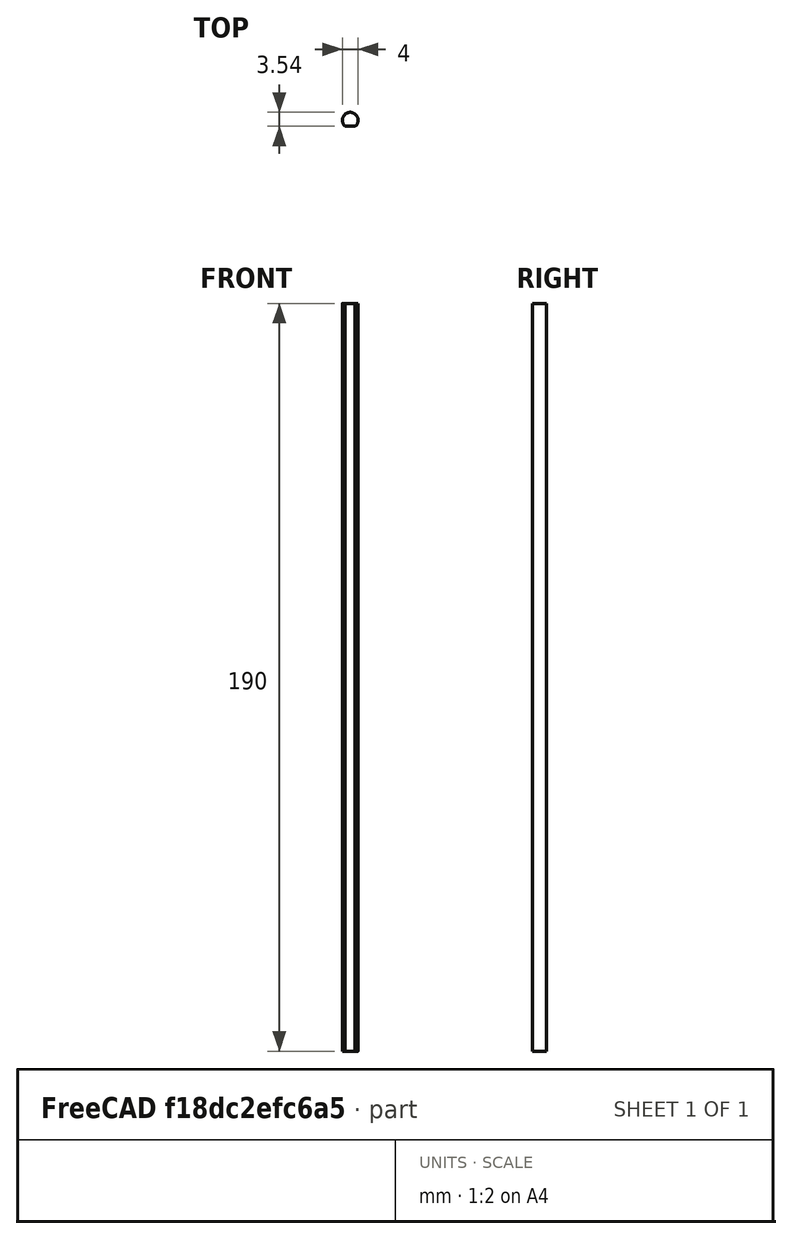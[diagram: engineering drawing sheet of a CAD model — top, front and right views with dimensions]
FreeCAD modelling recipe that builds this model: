
FCSTD DOCUMENT  (FreeCAD 0.16RUnknown)
Label: axle_cutted
License: All rights reserved
LicenseURL: http://en.wikipedia.org/wiki/All_rights_reserved
objects: Sketcher::SketchObject×1, PartDesign::Pad×1
note: 3 computed .brp shape members not serialized (recipe doc carries the construction recipe); baked Part::Feature solids carry a one-line shape summary decoded from their .brp

FEATURE [Sketcher::SketchObject] Sketch
  Placement = pos=(0,0,5) rot=(0,0,1;0rad)
  sketch-geometry (2):
    g0: ArcOfCircle CenterX=0 CenterY=0 CenterZ=0 NormalX=0 NormalY=0 NormalZ=1 Radius=2 StartAngle=5.40492 EndAngle=10.303
    g1: LineSegment StartX=-1.27698 StartY=-1.53926 StartZ=0 EndX=1.27698 EndY=-1.53926 EndZ=0
  constraints (6):
    c: Coincident(g0,g-1)
    c: Radius(g0) = 2
    c: Coincident(g1,g0)
    c: Horizontal(g1)
    c: DistanceX(g1,g1) = 2.55396
    c: Coincident(g0,g1)
FEATURE [PartDesign::Pad] Pad
  Length = 190
  Length2 = 100
  Placement = pos=(0,0,5) rot=(0,0,1;0rad)
  Sketch = -> Sketch
  Type = 0
